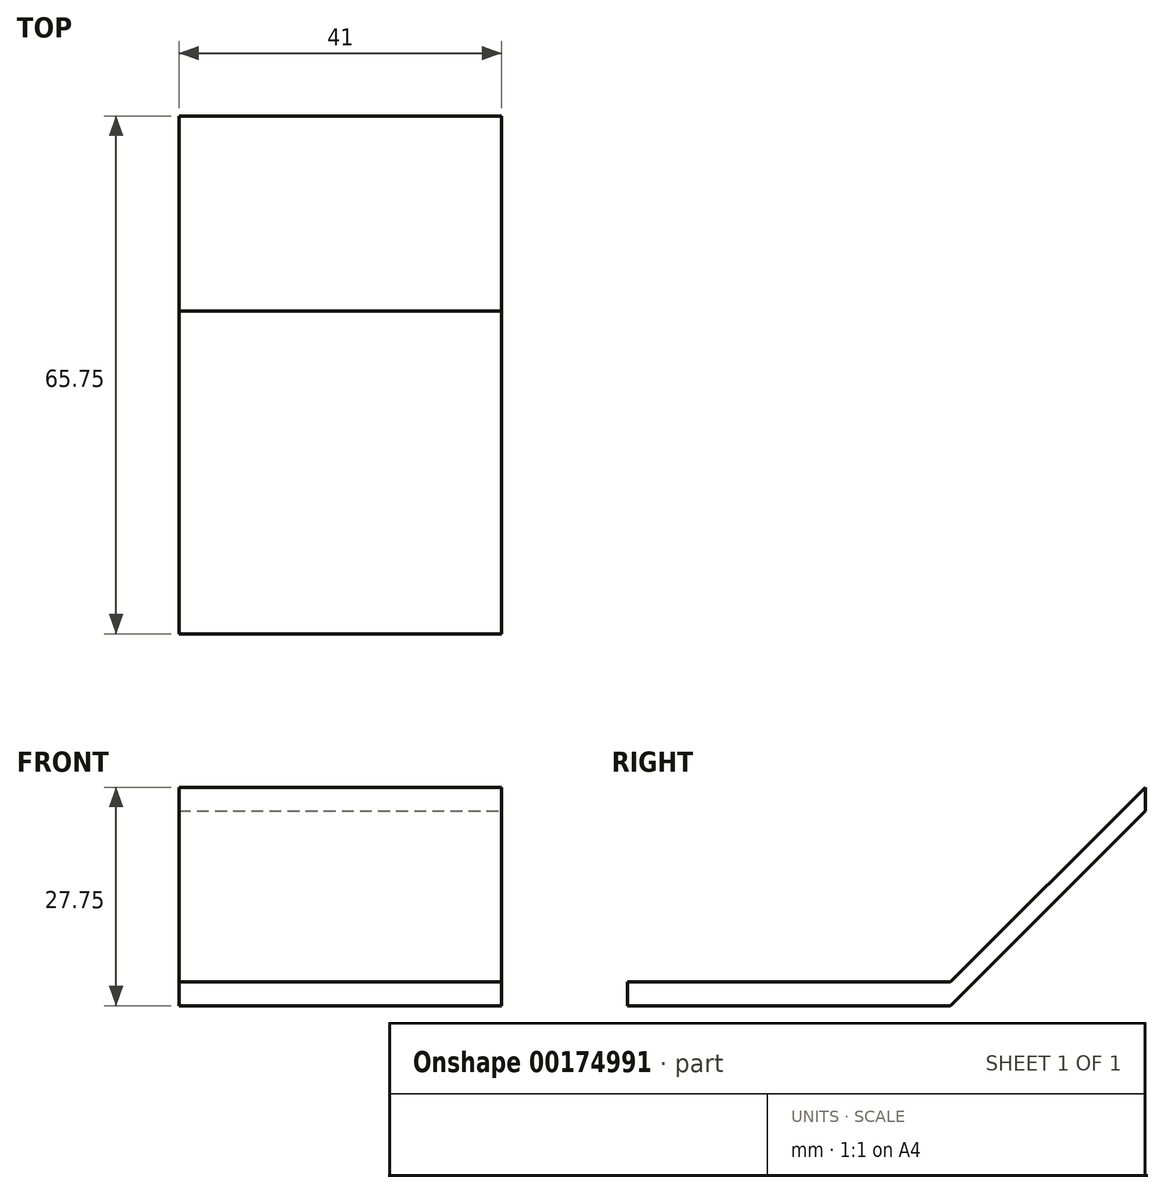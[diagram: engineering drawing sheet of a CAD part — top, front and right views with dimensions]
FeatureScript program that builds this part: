
annotation { "Feature Type Name" : "Feature", "Feature Type Description" : "" }
export const myFeature = defineFeature(function(context is Context, id is Id, definition is map)
    precondition{}
    {
        {
            var Q0;
            Q0=qCreatedBy(makeId("Top.planeOp"),FACE);
            var sketch = newSketch(context, id + "F0", { "sketchPlane" : qUnion([Q0])});
            skLineSegment(sketch, "E0.bottom", {"start": v(15.5, -15.5) * mm, "end": v(-15.5, -15.5) * mm});
            skLineSegment(sketch, "E0.top", {"start": v(15.5, 15.5) * mm, "end": v(-15.5, 15.5) * mm});
            skLineSegment(sketch, "E0.left", {"start": v(15.5, -15.5) * mm, "end": v(15.5, 15.5) * mm});
            skLineSegment(sketch, "E0.right", {"start": v(-15.5, -15.5) * mm, "end": v(-15.5, 15.5) * mm});
            skPoint(sketch, "E0.middle", {"position": v(0, 0) * mm});
            skLineSegment(sketch, "E1.0", {"start": v(20.5, -20.5) * mm, "end": v(20.5, 20.5) * mm});
            skLineSegment(sketch, "E1.1", {"start": v(20.5, -20.5) * mm, "end": v(-20.5, -20.5) * mm});
            skLineSegment(sketch, "E1.2", {"start": v(-20.5, -20.5) * mm, "end": v(-20.5, 20.5) * mm});
            skLineSegment(sketch, "E1.3", {"start": v(20.5, 20.5) * mm, "end": v(-20.5, 20.5) * mm});
            skSolve(sketch);
        }
        {
            var Q0;
            Q0=makeQuery(id+"F0.imprint","IMPRINT",FACE,{"disambiguationData":[TD([[makeQuery(id+"F0.imprint","IMPRINT",EDGE,{"derivedFrom":sQuery(id+"F0.wireOp",EDGE,"E0.bottom")}),1.0]])]});
            var Q1;
            Q1=makeQuery(id+"F0.imprint","IMPRINT",FACE,{"disambiguationData":[TD([[makeQuery(id+"F0.imprint","IMPRINT",EDGE,{"derivedFrom":sQuery(id+"F0.wireOp",EDGE,"E0.bottom")}),-1.0]])]});
            extrude(context, id + "F1", {"entities" : qUnion([Q0, Q1]), "depth" : 3 * mm});
        }
        {
            var Q0;
            Q0=makeQuery(id+"F1.opExtrude","SWEPT_FACE",FACE,{"disambiguationData":[OSD([sQuery(id+"F0.wireOp",EDGE,"E1.0")])]});
            var sketch = newSketch(context, id + "F3", { "sketchPlane" : qUnion([Q0])});
            skLineSegment(sketch, "E2", {"start": v(20.5, 0) * mm, "end": v(45.25, 24.75) * mm});
            skLineSegment(sketch, "E3", {"start": v(20.5, 3) * mm, "end": v(45.25, 27.75) * mm});
            skLineSegment(sketch, "E4", {"start": v(45.25, 24.75) * mm, "end": v(45.25, 27.75) * mm});
            skSolve(sketch);
        }
        {
            var Q0;
            Q0=makeQuery(id+"F3.imprint","IMPRINT",FACE,{"disambiguationData":[TD([[makeQuery(id+"F3.imprint","IMPRINT",EDGE,{"derivedFrom":sQuery(id+"F3.wireOp",EDGE,"E2")}),1.0]])]});
            extrude(context, id + "F2", {"entities" : qUnion([Q0]), "operationType" : NewBodyOperationType.ADD, "oppositeDirection" : true, "depth" : 41 * mm});
        }
    });
